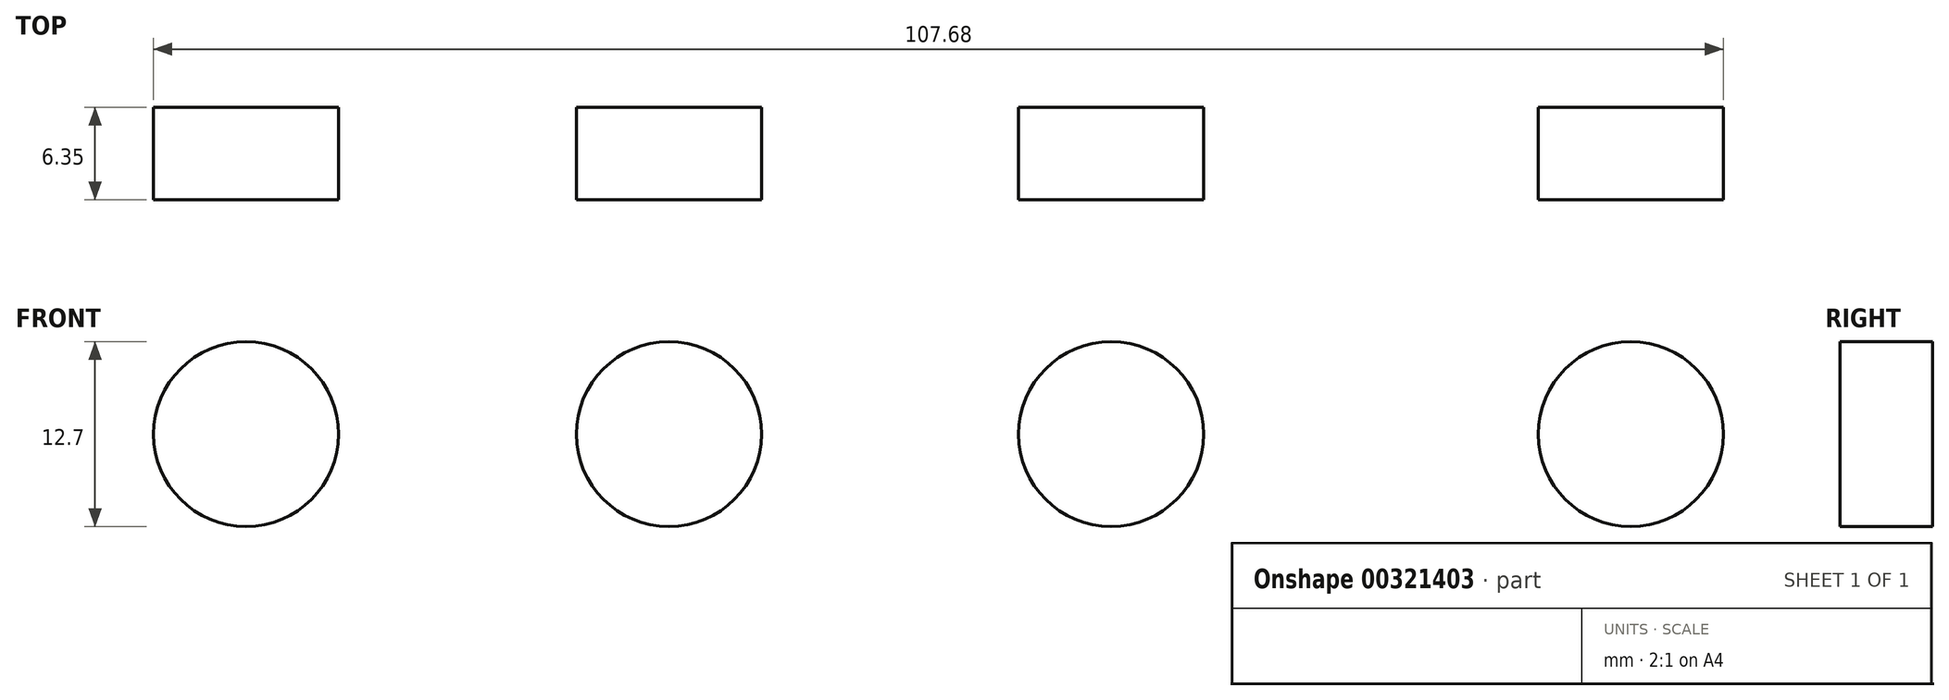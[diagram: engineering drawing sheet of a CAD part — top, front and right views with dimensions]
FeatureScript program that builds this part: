
annotation { "Feature Type Name" : "Feature", "Feature Type Description" : "" }
export const myFeature = defineFeature(function(context is Context, id is Id, definition is map)
    precondition{}
    {
        {
            var Q0;
            Q0=qCreatedBy(makeId("Front.planeOp"),FACE);
            var sketch = newSketch(context, id + "F0", { "sketchPlane" : qUnion([Q0])});
            skCircle(sketch, "E0", {"center": v(0, 0) * mm, "radius": 6.35 * mm});
            skCircle(sketch, "E1", {"center": v(35.64, 0) * mm, "radius": 6.35 * mm});
            skCircle(sketch, "E2", {"center": v(-30.34, 0) * mm, "radius": 6.35 * mm});
            skCircle(sketch, "E3", {"center": v(-59.34, 0) * mm, "radius": 6.35 * mm});
            skSolve(sketch);
        }
        {
            var Q0;
            Q0 = qSketchRegion(id + "F0", true);
            extrude(context, id + "F1", {"entities" : qUnion([Q0]), "depth" : 6.35 * mm});
        }
    });
